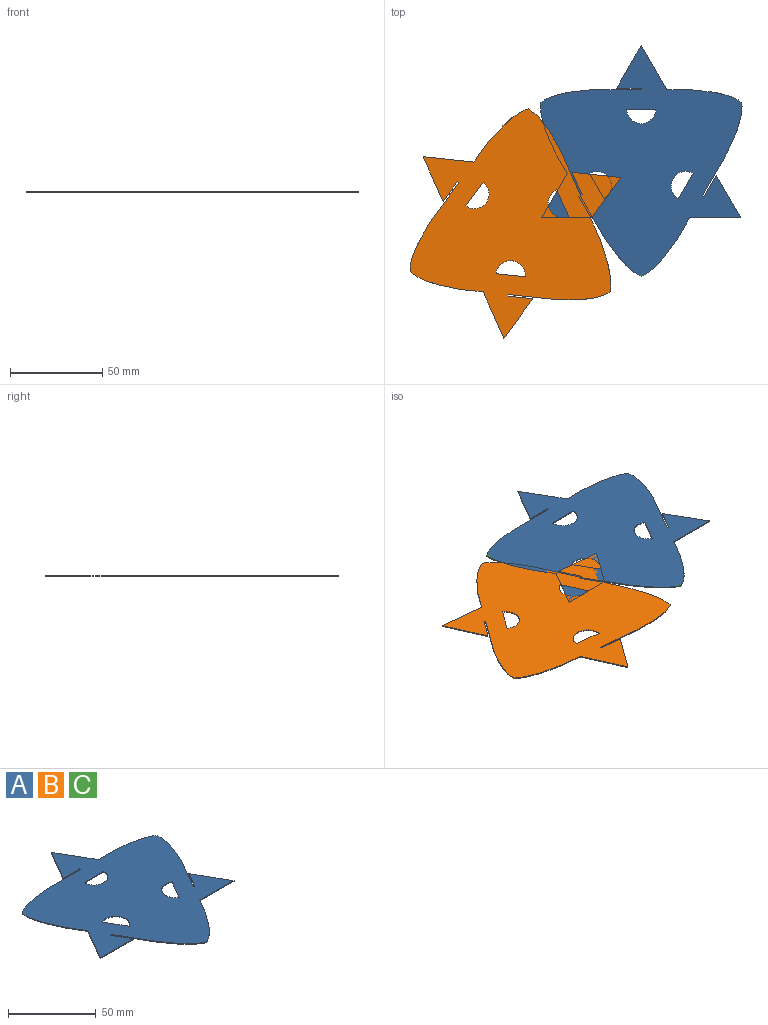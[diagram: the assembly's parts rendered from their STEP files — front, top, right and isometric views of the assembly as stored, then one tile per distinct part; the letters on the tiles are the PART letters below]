
ASSEMBLY  parts=3 mates=1
PART A: 32 faces, bbox 111.6x125.2x0.5 mm
  f0: plane 12.95x0.46mm, normal (0,1,0), area 5.9mm2, adj f1,f29,f30,f31
  f1: plane 23.99x13.85mm, normal (0.87,0.5,0), area 12.7mm2, adj f0,f2,f30,f31
  f2: plane 23.1x13.34mm, normal (-0.87,0.5,0), area 12.2mm2, adj f1,f3,f30,f31
  f3: plane 13.34x0.46mm, normal (0,-1,0), area 6.1mm2, adj f2,f4,f30,f31
  f4: plane 0.89x0.46mm, normal (-1,0,0), area 0.4mm2, adj f3,f5,f30,f31
  f5: plane 26.79x0.46mm, normal (0,1,0), area 12.3mm2, adj f4,f6,f30,f31
  f6: extruded ~27.69x6.88mm, area 13.2mm2, adj f5,f7,f30,f31
  f7: extruded ~27.42x8.05mm, area 13.2mm2, adj f6,f8,f30,f31
  f8: plane 11.21x6.47mm, normal (-0.87,-0.5,0), area 5.9mm2, adj f7,f9,f30,f31
  f9: plane 23.99x13.85mm, normal (-0.87,0.5,0), area 12.7mm2, adj f8,f10,f30,f31
  f10: plane 26.67x0.46mm, normal (0,-1,0), area 12.2mm2, adj f9,f11,f30,f31
  f11: plane 11.55x6.67mm, normal (0.87,0.5,0), area 6.1mm2, adj f10,f12,f30,f31
  f12: plane 0.77x0.46mm, normal (0.5,-0.87,0), area 0.4mm2, adj f11,f13,f30,f31
  f13: plane 23.21x13.4mm, normal (-0.87,-0.5,0), area 12.3mm2, adj f12,f14,f30,f31
  f14: extruded ~20.54x19.81mm, area 13.2mm2, adj f13,f15,f30,f31
  f15: extruded ~20.54x19.81mm, area 13.2mm2, adj f14,f16,f30,f31
  f16: plane 11.21x6.47mm, normal (0.87,-0.5,0), area 5.9mm2, adj f15,f17,f30,f31
  f17: plane 27.7x0.46mm, normal (0,-1,0), area 12.7mm2, adj f16,f18,f30,f31
  f18: plane 23.1x13.34mm, normal (0.87,0.5,0), area 12.2mm2, adj f17,f19,f30,f31
  f19: plane 11.55x6.67mm, normal (-0.87,0.5,0), area 6.1mm2, adj f18,f20,f30,f31
  f20: plane 0.77x0.46mm, normal (0.5,0.87,0), area 0.4mm2, adj f19,f21,f30,f31
  f21: plane 23.21x13.4mm, normal (0.87,-0.5,0), area 12.3mm2, adj f20,f22,f30,f31
  f22: extruded ~27.42x8.05mm, area 13.2mm2, adj f21,f29,f30,f31
  f23: cylinder r=7.94mm len=15.88mm, axis (0,0,-1), area 11.4mm2, adj f26,f30,f31
  f24: cylinder r=7.94mm len=14.81mm, axis (0,0,-1), area 11.4mm2, adj f27,f30,f31
  f25: plane 13.75x7.94mm, normal (0.87,0.5,0), area 7.3mm2, adj f28,f30,f31
  f26: plane 15.88x0.46mm, normal (0,-1,0), area 7.3mm2, adj f23,f30,f31
  f27: plane 13.75x7.94mm, normal (-0.87,0.5,0), area 7.3mm2, adj f24,f30,f31
  f28: cylinder r=7.94mm len=14.81mm, axis (0,0,-1), area 11.4mm2, adj f25,f30,f31
  f29: extruded ~27.69x6.88mm, area 13.2mm2, adj f0,f22,f30,f31
  f30: plane 125.24x111.59mm, normal (0,0,1), area 7697.8mm2, adj f0,f1,f2,f3,f4,f5,f6,f7
  f31: plane 125.24x111.59mm, normal (0,0,-1), area 7697.8mm2, adj f0,f1,f2,f3,f4,f5,f6,f7
PART B: same geometry as A
PART C: same geometry as A
PLACE A t=(-75.25,32.64,-0.23)mm
PLACE B rot(axis=(0,0,1),54deg) t=(-117.99,10.86,-0.23)mm
PLACE C t=(-75.25,32.64,-0.23)mm
MATE revolute B.f31 <-> A.f31  axis (0,0,1) through (-75.25,-20.19,-0.23)mm
